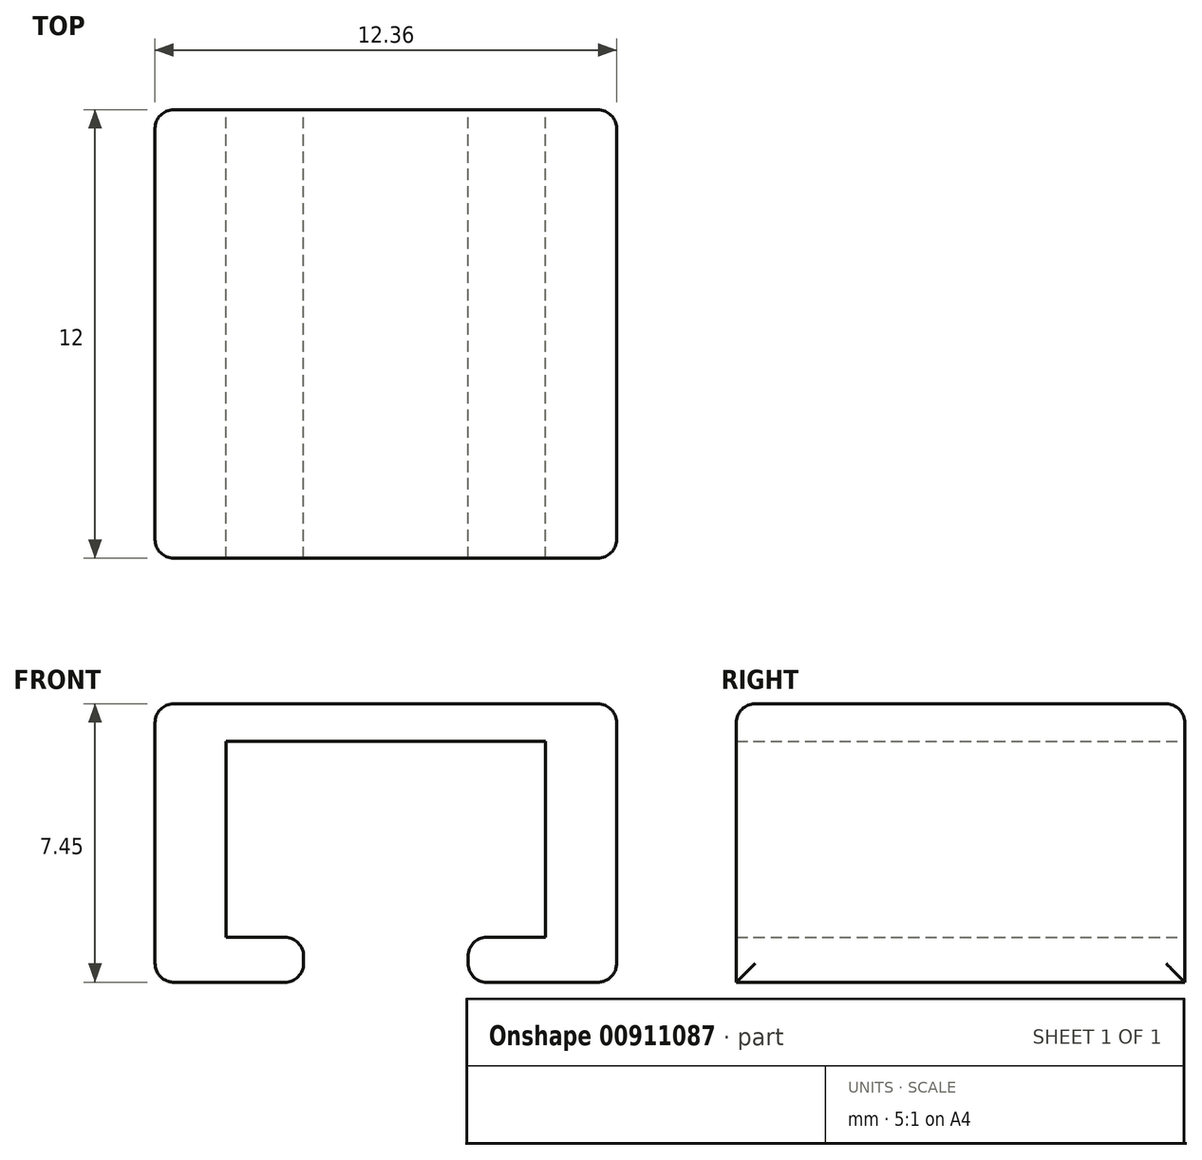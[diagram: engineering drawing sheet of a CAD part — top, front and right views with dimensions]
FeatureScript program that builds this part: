
annotation { "Feature Type Name" : "Feature", "Feature Type Description" : "" }
export const myFeature = defineFeature(function(context is Context, id is Id, definition is map)
    precondition{}
    {
        {
            var Q0;
            Q0=qCreatedBy(makeId("Front.planeOp"),FACE);
            var sketch = newSketch(context, id + "F0", { "sketchPlane" : qUnion([Q0])});
            skLineSegment(sketch, "E0.bottom", {"start": v(6.17, 2.9) * mm, "end": v(-6.18, 2.9) * mm});
            skLineSegment(sketch, "E0.top", {"start": v(6.18, -4.55) * mm, "end": v(-6.17, -4.55) * mm});
            skLineSegment(sketch, "E0.left", {"start": v(6.18, 2.9) * mm, "end": v(6.18, -4.55) * mm});
            skLineSegment(sketch, "E0.right", {"start": v(-6.17, 2.9) * mm, "end": v(-6.17, -4.55) * mm});
            skPoint(sketch, "E0.middle", {"position": v(0, -0.83) * mm});
            skLineSegment(sketch, "E1.0", {"start": v(4.28, -3.35) * mm, "end": v(-4.27, -3.35) * mm});
            skLineSegment(sketch, "E2", {"start": v(0, -3.35) * mm, "end": v(0, -4.55) * mm});
            skLineSegment(sketch, "E3.0", {"start": v(-2.2, -3.35) * mm, "end": v(-2.2, -4.55) * mm});
            skLineSegment(sketch, "E4.MirrorCS", {"start": v(2.2, -3.35) * mm, "end": v(2.2, -4.55) * mm});
            skLineSegment(sketch, "E5.0", {"start": v(-4.28, 1.9) * mm, "end": v(-4.27, -3.35) * mm});
            skLineSegment(sketch, "E6.0", {"start": v(4.27, 1.9) * mm, "end": v(4.28, -3.35) * mm});
            skLineSegment(sketch, "E7.0", {"start": v(4.27, 1.9) * mm, "end": v(-4.28, 1.9) * mm});
            skPoint(sketch, "E8.orphan", {"position": v(6.18, -3.35) * mm});
            skPoint(sketch, "E9.orphan", {"position": v(-6.17, -3.35) * mm});
            skLineSegment(sketch, "E10", {"start": v(0, 2.9) * mm, "end": v(0, 1.9) * mm, "construction": true});
            skSolve(sketch);
        }
        {
            var Q0;
            Q0=makeQuery(id+"F0.imprint","IMPRINT",FACE,{"disambiguationData":[TD([[makeQuery(id+"F0.imprint","IMPRINT",EDGE,{"derivedFrom":sQuery(id+"F0.wireOp",EDGE,"E0.bottom")}),1.0]])]});
            extrude(context, id + "F1", {"entities" : qUnion([Q0]), "depth" : 12 * mm, "symmetric" : true});
        }
        {
            var Q0;
            Q0=makeQuery(id+"F1.opExtrude","SWEPT_EDGE",EDGE,{"disambiguationData":[OSD([sQuery(id+"F0.wireOp",EDGE,"E0.top"),sQuery(id+"F0.wireOp",EDGE,"E3.0")])]});
            var Q1;
            Q1=makeQuery(id+"F1.opExtrude","SWEPT_EDGE",EDGE,{"disambiguationData":[OSD([sQuery(id+"F0.wireOp",EDGE,"E0.top"),sQuery(id+"F0.wireOp",EDGE,"E4.MirrorCS")])]});
            var Q2;
            Q2=makeQuery(id+"F1.opExtrude","SWEPT_EDGE",EDGE,{"disambiguationData":[OSD([sQuery(id+"F0.wireOp",EDGE,"E1.0"),sQuery(id+"F0.wireOp",EDGE,"E3.0")])]});
            var Q3;
            Q3=makeQuery(id+"F1.opExtrude","SWEPT_EDGE",EDGE,{"disambiguationData":[OSD([sQuery(id+"F0.wireOp",EDGE,"E1.0"),sQuery(id+"F0.wireOp",EDGE,"E4.MirrorCS")])]});
            fillet(context, id + "F2", {"entities" : qUnion([Q0, Q1, Q2, Q3]), "radius" : .5 * mm, "tangentPropagation" : true, "allowEdgeOverflow" : false});
        }
        {
            var Q0;
            Q0=makeQuery(id+"F1.opExtrude","SWEPT_FACE",FACE,{"disambiguationData":[OSD([sQuery(id+"F0.wireOp",EDGE,"E0.left")])]});
            var Q1;
            Q1=makeQuery(id+"F1.opExtrude","SWEPT_FACE",FACE,{"disambiguationData":[OSD([sQuery(id+"F0.wireOp",EDGE,"E0.bottom")])]});
            var Q2;
            Q2=makeQuery(id+"F1.opExtrude","SWEPT_FACE",FACE,{"disambiguationData":[OSD([sQuery(id+"F0.wireOp",EDGE,"E0.right")])]});
            fillet(context, id + "F3", {"entities" : qUnion([Q0, Q1, Q2]), "radius" : .5 * mm, "tangentPropagation" : true, "allowEdgeOverflow" : false});
        }
    });
